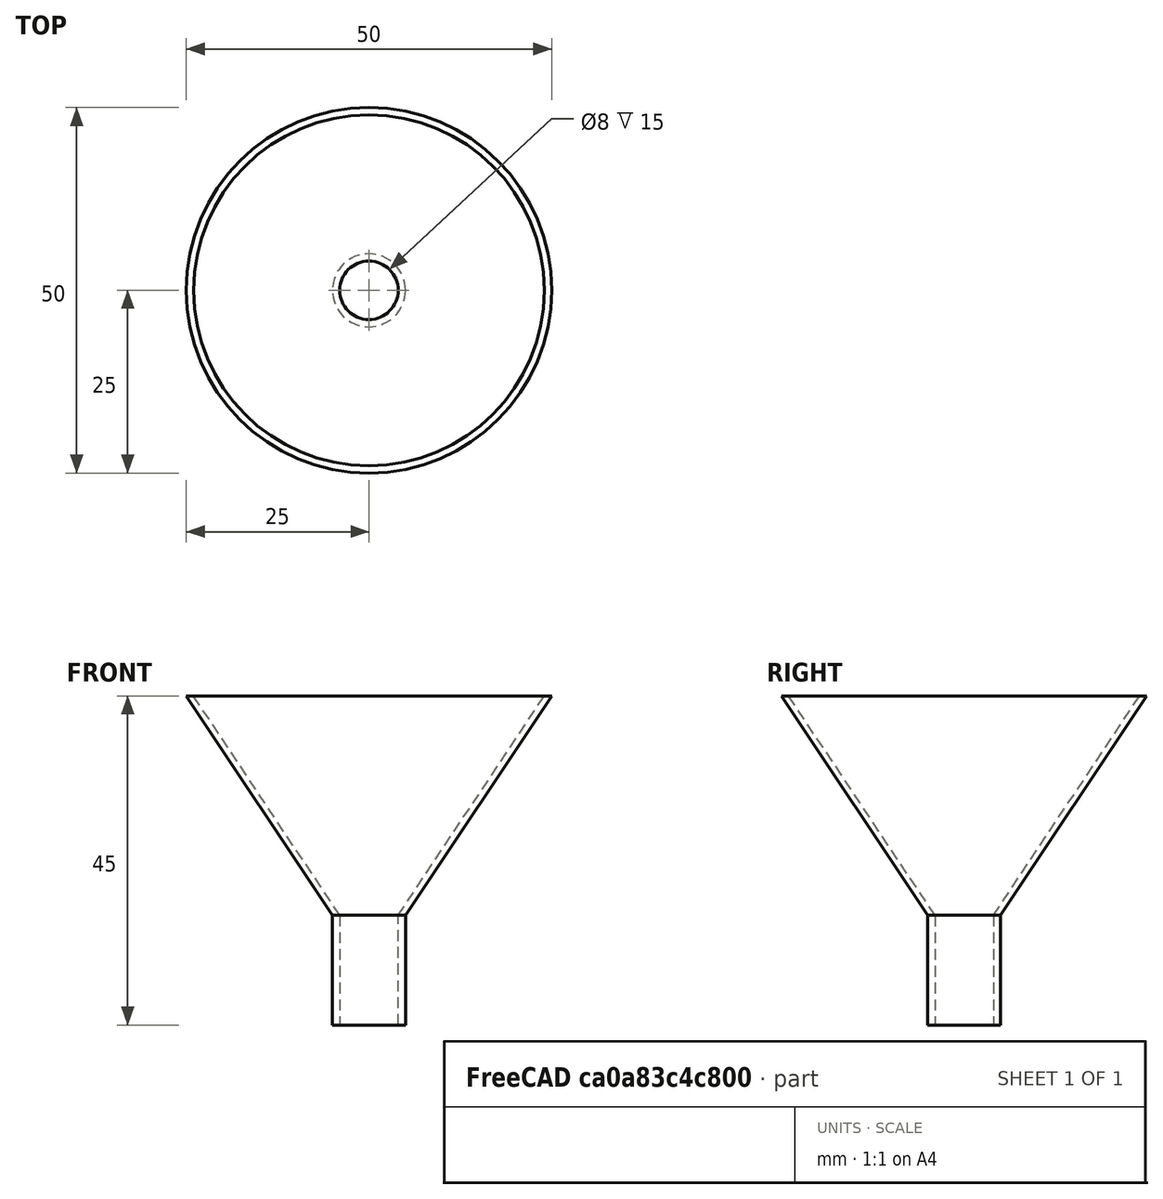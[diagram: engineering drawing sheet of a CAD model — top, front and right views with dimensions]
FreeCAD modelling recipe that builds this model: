
FCSTD DOCUMENT  (FreeCAD 0.21R33771 (Git))
Label: OJT1_T14R03_embut
License: All rights reserved
LicenseURL: http://en.wikipedia.org/wiki/All_rights_reserved
objects: Part::Cylinder×2, Part::Cut×2, Part::Cone×2, Part::MultiFuse×1
note: 7 computed .brp shape members not serialized (recipe doc carries the construction recipe); baked Part::Feature solids carry a one-line shape summary decoded from their .brp

FEATURE [Part::Cylinder] Cylinder
  Angle = 360
  AttacherType = Attacher::AttachEngine3D
  FirstAngle = 0
  Height = 15
  Radius = 5
  SecondAngle = 0
FEATURE [Part::Cylinder] Cylinder001
  Angle = 360
  AttacherType = Attacher::AttachEngine3D
  FirstAngle = 0
  Height = 15
  Radius = 4
  SecondAngle = 0
FEATURE [Part::Cut] Cut
  Base = -> Cylinder
  Refine = true
  Tool = -> Cylinder001
FEATURE [Part::Cone] Cone
  Angle = 360
  AttacherType = Attacher::AttachEngine3D
  Height = 30
  Placement = pos=(0,0,15) rot=(0,0,1;0rad)
  Radius1 = 5
  Radius2 = 25
FEATURE [Part::Cone] Cone001
  Angle = 360
  AttacherType = Attacher::AttachEngine3D
  Height = 30
  Placement = pos=(0,0,15) rot=(0,0,1;0rad)
  Radius1 = 4
  Radius2 = 24
FEATURE [Part::Cut] Cut001
  Base = -> Cone
  Refine = true
  Tool = -> Cone001
FEATURE [Part::MultiFuse] Fusion  label="embut"
  Refine = true
  Shapes = -> [Cut,Cut001]
